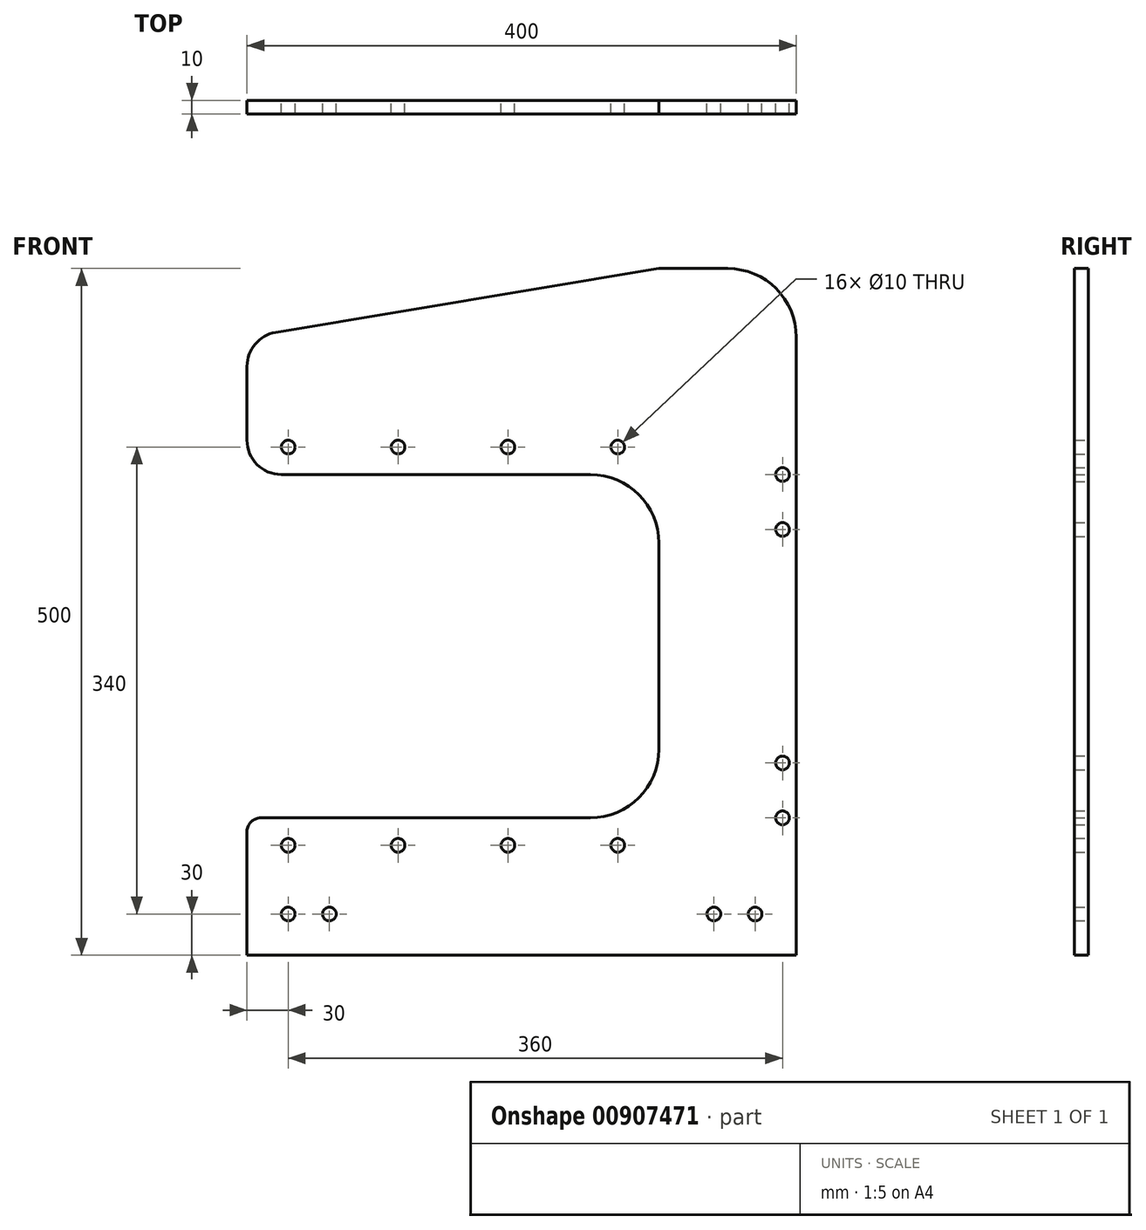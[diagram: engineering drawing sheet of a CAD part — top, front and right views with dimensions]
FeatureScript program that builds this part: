
annotation { "Feature Type Name" : "Feature", "Feature Type Description" : "" }
export const myFeature = defineFeature(function(context is Context, id is Id, definition is map)
    precondition{}
    {
        {
            var Q0;
            Q0=qCreatedBy(makeId("Front.planeOp"),FACE);
            var sketch = newSketch(context, id + "F0", { "sketchPlane" : qUnion([Q0])});
            skLineSegment(sketch, "E0", {"start": v(-400, 0) * mm, "end": v(0, 0) * mm});
            skLineSegment(sketch, "E1", {"start": v(0, 0) * mm, "end": v(0, 450) * mm});
            skLineSegment(sketch, "E2", {"start": v(-50, 500) * mm, "end": v(-100, 500) * mm});
            skLineSegment(sketch, "E3", {"start": v(-400, 428.82) * mm, "end": v(-400, 375) * mm});
            skLineSegment(sketch, "E4", {"start": v(-375, 350) * mm, "end": v(-150, 350) * mm});
            skLineSegment(sketch, "E5", {"start": v(-100, 300) * mm, "end": v(-100, 150) * mm});
            skLineSegment(sketch, "E6", {"start": v(-150, 100) * mm, "end": v(-390, 100) * mm});
            skLineSegment(sketch, "E7", {"start": v(-400, 90) * mm, "end": v(-400, 0) * mm});
            skPoint(sketch, "E8.visualSharp", {"position": v(-100, 100) * mm});
            skArc(sketch, "E8.filletArc", {"start": v(-150, 100) * mm, "mid": v(-114.64, 114.64) * mm, "end": v(-100, 150) * mm});
            skPoint(sketch, "E9.visualSharp", {"position": v(-100, 350) * mm});
            skArc(sketch, "E9.filletArc", {"start": v(-100, 300) * mm, "mid": v(-114.64, 335.36) * mm, "end": v(-150, 350) * mm});
            skPoint(sketch, "E10.visualSharp", {"position": v(-400, 100) * mm});
            skArc(sketch, "E10.filletArc", {"start": v(-390, 100) * mm, "mid": v(-397.07, 97.07) * mm, "end": v(-400, 90) * mm});
            skPoint(sketch, "E11.visualSharp", {"position": v(-400, 350) * mm});
            skArc(sketch, "E11.filletArc", {"start": v(-400, 375) * mm, "mid": v(-392.68, 357.32) * mm, "end": v(-375, 350) * mm});
            skLineSegment(sketch, "E12", {"start": v(-379.1, 453.48) * mm, "end": v(-100, 500) * mm});
            skPoint(sketch, "E13.visualSharp", {"position": v(-400, 450) * mm});
            skArc(sketch, "E13.filletArc", {"start": v(-379.1, 453.48) * mm, "mid": v(-394.08, 444.98) * mm, "end": v(-400, 428.82) * mm});
            skPoint(sketch, "E14.visualSharp", {"position": v(0, 500) * mm});
            skArc(sketch, "E14.filletArc", {"start": v(0, 450) * mm, "mid": v(-14.64, 485.36) * mm, "end": v(-50, 500) * mm});
            skCircle(sketch, "E15", {"center": v(-370, 80) * mm, "radius": 5 * mm});
            skCircle(sketch, "E16", {"center": v(-290, 80) * mm, "radius": 5 * mm});
            skCircle(sketch, "E17", {"center": v(-210, 80) * mm, "radius": 5 * mm});
            skCircle(sketch, "E18", {"center": v(-130, 80) * mm, "radius": 5 * mm});
            skCircle(sketch, "E19.0.1.0", {"center": v(-370, 370) * mm, "radius": 5 * mm});
            skCircle(sketch, "E19.0.1.1", {"center": v(-290, 370) * mm, "radius": 5 * mm});
            skCircle(sketch, "E19.0.1.2", {"center": v(-210, 370) * mm, "radius": 5 * mm});
            skCircle(sketch, "E19.0.1.3", {"center": v(-130, 370) * mm, "radius": 5 * mm});
            skLineSegment(sketch, "E19.direction1", {"start": v(-370, 80) * mm, "end": v(-550, 80) * mm, "construction": true});
            skLineSegment(sketch, "E19.direction2", {"start": v(-370, 80) * mm, "end": v(-370, 370) * mm, "construction": true});
            skCircle(sketch, "E20", {"center": v(-10, 350) * mm, "radius": 5 * mm});
            skCircle(sketch, "E21", {"center": v(-10, 310) * mm, "radius": 5 * mm});
            skCircle(sketch, "E22", {"center": v(-10, 140) * mm, "radius": 5 * mm});
            skCircle(sketch, "E23", {"center": v(-10, 100) * mm, "radius": 5 * mm});
            skCircle(sketch, "E24", {"center": v(-60, 30) * mm, "radius": 5 * mm});
            skCircle(sketch, "E25", {"center": v(-30, 30) * mm, "radius": 5 * mm});
            skCircle(sketch, "E26", {"center": v(-370, 30) * mm, "radius": 5 * mm});
            skCircle(sketch, "E27", {"center": v(-340, 30) * mm, "radius": 5 * mm});
            skSolve(sketch);
        }
        {
            var Q0;
            Q0 = qSketchRegion(id + "F0", true);
            extrude(context, id + "F1", {"entities" : qUnion([Q0]), "depth" : 10 * mm, "offsetDistance" : 25 * mm});
        }
    });
